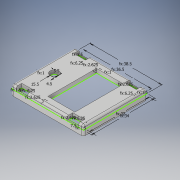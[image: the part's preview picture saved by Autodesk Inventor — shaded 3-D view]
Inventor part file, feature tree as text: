
AUTODESK INVENTOR PART (.ipt)
format: ipt  version: 2019 (Build 230136000, 136)  size: 286,208 bytes
history: native  units: mm
features: extrude x9, sketch x3, fillet x3
ambient origin geometry x8: Origin, YZ Plane, XZ Plane, XY Plane, X Axis, Y Axis, Z Axis, Center Point
bodies: Solid1 (feature_tree)
feature tree (15):
  sketch  "Sketch1"  dims[d0=36.5mm d1=32.0mm d4=38.5mm]
  extrude  "Extrusion1"  Depth=32.0mm
  fillet  "Fillet1"  Radius=38.5mm
  sketch  "Sketch3"  dims[d5=34.0mm d6=1.0mm]
  extrude  "Extrusion2"  Depth=1.0mm
  extrude  "Extrusion6"  Depth=2.125mm TaperAngle=0.0deg
  extrude  "Extrusion7"  Depth=1.0mm
  extrude  "Extrusion8"  Depth=2.125mm TaperAngle=0.0deg
  extrude  "Extrusion9"  Depth=1.5mm
  fillet  "Fillet3"  Radius=1.5mm
  extrude  "Extrusion16"  Depth=6.25mm
  fillet  "Fillet5"  Radius=6.25mm
  extrude  "Extrusion17"  Depth=2.625mm
  extrude  "Extrusion18"  Depth=2.625mm
  sketch  "Sketch11"  dims[d7=1.0mm d8=2.125mm d9=0.0mm d13=1.0mm d17=2.125mm d18=0.0mm d31=1.5mm d33=1.5mm d34=6.25mm d36=6.25mm d37=2.625mm d39=2.625mm d42=1.5mm d43=6.25mm d44=2.625mm d45=2.125mm d46=0.0mm d47=2.125mm d48=0.0mm d49=2.125mm d50=0.0mm d52=1.75mm d53=0.0mm d54=1.0mm d55=6.25mm d56=6.25mm d69=7.5mm d74=3.0mm d75=0.0mm d76=1.0mm d80=10.0mm d81=0.0mm d82=3.0mm d84=6.25mm d85=1.5mm d88=3.0mm d89=4.5mm d90=15.5mm d91=5.5mm d92=10.0mm d93=0.0mm]
